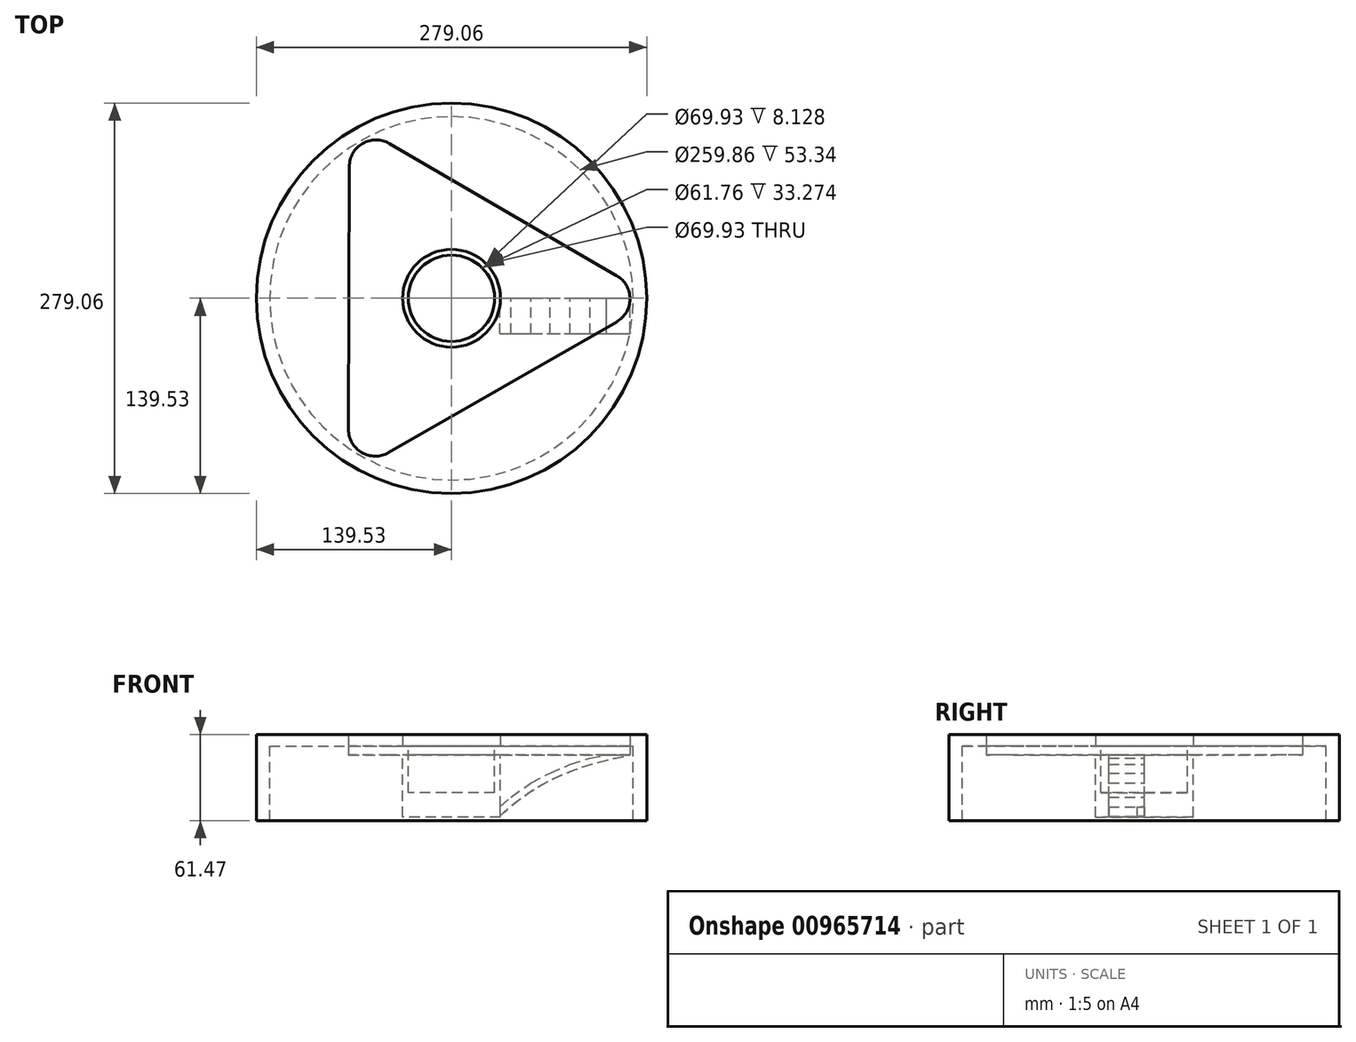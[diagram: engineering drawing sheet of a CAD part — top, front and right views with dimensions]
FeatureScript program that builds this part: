
annotation { "Feature Type Name" : "Feature", "Feature Type Description" : "" }
export const myFeature = defineFeature(function(context is Context, id is Id, definition is map)
    precondition{}
    {
        {
            var Q0;
            Q0=qCreatedBy(makeId("Top.planeOp"),FACE);
            var sketch = newSketch(context, id + "F0", { "sketchPlane" : qUnion([Q0])});
            skCircle(sketch, "E0.cCircle", {"center": v(0, 0) * mm, "radius": 73.32 * mm, "construction": true});
            skLineSegment(sketch, "E0.0", {"start": v(-72.94, 127.22) * mm, "end": v(146.65, -0.45) * mm});
            skLineSegment(sketch, "E0.1", {"start": v(146.65, -0.45) * mm, "end": v(-73.71, -126.78) * mm});
            skLineSegment(sketch, "E0.2", {"start": v(-73.71, -126.78) * mm, "end": v(-72.94, 127.22) * mm});
            skPoint(sketch, "E0.0.midPoint", {"position": v(36.86, 63.39) * mm});
            skSolve(sketch);
        }
        {
            var Q0;
            Q0=makeQuery(id+"F0.imprint","IMPRINT",FACE,{"disambiguationData":[TD([[makeQuery(id+"F0.imprint","IMPRINT",EDGE,{"derivedFrom":sQuery(id+"F0.wireOp",EDGE,"E0.0")}),-1.0]])]});
            extrude(context, id + "F1", {"entities" : qUnion([Q0]), "depth" : 6.35 * mm, "offsetDistance" : 25.4 * mm});
        }
        {
            var Q0;
            Q0=makeQuery(id+"F1.opExtrude","SWEPT_EDGE",EDGE,{"disambiguationData":[OSD([sQuery(id+"F0.wireOp",EDGE,"E0.1"),sQuery(id+"F0.wireOp",EDGE,"E0.2")])]});
            var Q1;
            Q1=makeQuery(id+"F1.opExtrude","SWEPT_EDGE",EDGE,{"disambiguationData":[OSD([sQuery(id+"F0.wireOp",EDGE,"E0.0"),sQuery(id+"F0.wireOp",EDGE,"E0.1")])]});
            var Q2;
            Q2=makeQuery(id+"F1.opExtrude","SWEPT_EDGE",EDGE,{"disambiguationData":[OSD([sQuery(id+"F0.wireOp",EDGE,"E0.0"),sQuery(id+"F0.wireOp",EDGE,"E0.2")])]});
            fillet(context, id + "F2", {"entities" : qUnion([Q0, Q1, Q2]), "radius" : 19.05 * mm, "tangentPropagation" : true, "allowEdgeOverflow" : false});
        }
        {
            var Q0;
            Q0=makeQuery(id+"F1.opExtrude","CAP_FACE",FACE,{"disambiguationData":[OSD([sQuery(id+"F0.wireOp",EDGE,"E0.0"),sQuery(id+"F0.wireOp",EDGE,"E0.1"),sQuery(id+"F0.wireOp",EDGE,"E0.2")])],"isStart":false});
            var sketch = newSketch(context, id + "F3", { "sketchPlane" : qUnion([Q0])});
            skCircle(sketch, "E1", {"center": v(0, 0) * mm, "radius": 34.96 * mm});
            skSolve(sketch);
        }
        {
            var Q0;
            Q0=makeQuery(id+"F3.imprint","IMPRINT",FACE,{"disambiguationData":[TD([[makeQuery(id+"F3.imprint","IMPRINT",EDGE,{"derivedFrom":sQuery(id+"F3.wireOp",EDGE,"E1")}),1.0]])]});
            extrude(context, id + "F4", {"entities" : qUnion([Q0]), "operationType" : NewBodyOperationType.ADD, "oppositeDirection" : true, "depth" : 50.8 * mm, "offsetDistance" : 25.4 * mm});
        }
        {
            var Q0;
            Q0=makeQuery(id+"F3.imprint","IMPRINT",FACE,{"disambiguationData":[TD([[makeQuery(id+"F3.imprint","IMPRINT",EDGE,{"derivedFrom":sQuery(id+"F3.wireOp",EDGE,"E1")}),1.0]])]});
            var sketch = newSketch(context, id + "F5", { "sketchPlane" : qUnion([Q0])});
            skCircle(sketch, "E2", {"center": v(0, 0) * mm, "radius": 30.88 * mm});
            skSolve(sketch);
        }
        {
            var Q0;
            Q0=makeQuery(id+"F5.imprint","IMPRINT",FACE,{"disambiguationData":[TD([[makeQuery(id+"F5.imprint","IMPRINT",EDGE,{"derivedFrom":sQuery(id+"F5.wireOp",EDGE,"E2")}),1.0]])]});
            extrude(context, id + "F6", {"entities" : qUnion([Q0]), "operationType" : NewBodyOperationType.REMOVE, "oppositeDirection" : true, "depth" : 33.27 * mm, "offsetDistance" : 25.4 * mm});
        }
        {
            var Q0;
            Q0=makeQuery(id+"F3.imprint","IMPRINT",FACE,{"disambiguationData":[TD([[makeQuery(id+"F3.imprint","IMPRINT",EDGE,{"derivedFrom":sQuery(id+"F3.wireOp",EDGE,"E1")}),-1.0]])]});
            var sketch = newSketch(context, id + "F7", { "sketchPlane" : qUnion([Q0])});
            skCircle(sketch, "E3", {"center": v(0, 0) * mm, "radius": 139.53 * mm});
            skSolve(sketch);
        }
        {
            var Q0;
            Q0=makeQuery(id+"F7.imprint","IMPRINT",FACE,{"disambiguationData":[TD([[makeQuery(id+"F7.imprint","IMPRINT",EDGE,{"derivedFrom":sQuery(id+"F7.wireOp",EDGE,"E3")}),1.0]])]});
            var Q1;
            Q1=makeQuery(id+"F3.imprint","IMPRINT",FACE,{"disambiguationData":[TD([[makeQuery(id+"F3.imprint","IMPRINT",EDGE,{"derivedFrom":sQuery(id+"F3.wireOp",EDGE,"E1")}),-1.0]])]});
            extrude(context, id + "F8", {"entities" : qUnion([Q0, Q1]), "depth" : 8.13 * mm, "offsetDistance" : 25.4 * mm});
        }
        {
            var Q0;
            Q0=makeQuery(id+"F8.opExtrude","CAP_FACE",FACE,{"disambiguationData":[OSD([sQuery(id+"F0.wireOp",EDGE,"E0.0"),sQuery(id+"F0.wireOp",EDGE,"E0.1"),sQuery(id+"F0.wireOp",EDGE,"E0.2"),sQuery(id+"F7.wireOp",EDGE,"E3")])],"isStart":true});
            var sketch = newSketch(context, id + "F9", { "sketchPlane" : qUnion([Q0])});
            skCircle(sketch, "E4", {"center": v(0, 0) * mm, "radius": 129.93 * mm});
            skSolve(sketch);
        }
        {
            var Q0;
            Q0=makeQuery(id+"F9.imprint","IMPRINT",FACE,{"disambiguationData":[TD([[makeQuery(id+"F9.imprint","IMPRINT",EDGE,{"derivedFrom":sQuery(id+"F9.wireOp",EDGE,"E4")}),-1.0]])]});
            extrude(context, id + "F10", {"entities" : qUnion([Q0]), "operationType" : NewBodyOperationType.ADD, "depth" : 53.34 * mm, "offsetDistance" : 25.4 * mm});
        }
        {
            var Q0;
            Q0=qCreatedBy(makeId("Front.planeOp"),FACE);
            var sketch = newSketch(context, id + "F11", { "sketchPlane" : qUnion([Q0])});
            skFitSpline(sketch, "E5", {"points": [v(34.62, -43.82) * mm, v(43.73, -35.6) * mm, v(62.17, -22.72) * mm, v(79.86, -13.95) * mm, v(93.4, -8.76) * mm, v(115.3, -2.71) * mm, v(127.68, 0) * mm], "startDerivative": vector(57.86, 54.4) * mm, "endDerivative": vector(68.44, 23.35) * mm});
            skLineSegment(sketch, "E6", {"start": v(34.62, -37.27) * mm, "end": v(42.5, -30.12) * mm});
            skLineSegment(sketch, "E7", {"start": v(42.5, -30.12) * mm, "end": v(56.81, -20.1) * mm});
            skLineSegment(sketch, "E8", {"start": v(56.81, -20.1) * mm, "end": v(70.4, -12.94) * mm});
            skLineSegment(sketch, "E9", {"start": v(70.4, -12.94) * mm, "end": v(84.9, -6.86) * mm});
            skLineSegment(sketch, "E10", {"start": v(84.9, -6.86) * mm, "end": v(99.03, -2.39) * mm});
            skLineSegment(sketch, "E11", {"start": v(99.03, -2.39) * mm, "end": v(110.66, 0) * mm});
            skLineSegment(sketch, "E12", {"start": v(110.66, 0) * mm, "end": v(127.68, 0) * mm});
            skLineSegment(sketch, "E13", {"start": v(34.62, -37.27) * mm, "end": v(34.62, -43.82) * mm});
            skSolve(sketch);
        }
        {
            var Q0;
            Q0 = qSketchRegion(id + "F11", true);
            extrude(context, id + "F12", {"entities" : qUnion([Q0]), "depth" : 25.4 * mm, "offsetDistance" : 25.4 * mm});
        }
    });
